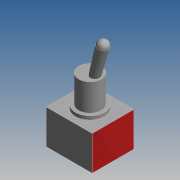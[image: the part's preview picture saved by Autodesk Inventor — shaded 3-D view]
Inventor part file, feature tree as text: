
AUTODESK INVENTOR PART (.ipt)
format: ipt  version: 2019 (Build 230136000, 136)  size: 237,056 bytes
history: native  units: mm
features: sketch x4, extrude x3, revolve x1, fillet x1
ambient origin geometry x8: Origin, YZ Plane, XZ Plane, XY Plane, X Axis, Y Axis, Z Axis, Center Point
bodies: Solid1 (feature_tree)
feature tree (9):
  extrude  "Extrusion1"  Depth=11.5mm
  extrude  "Extrusion2"  Depth=9.5mm
  extrude  "Extrusion3"  Depth=1.0mm
  revolve  "Revolution1"  Angle=15.0deg
  fillet  "Fillet1"  Radius=5.0mm
  sketch  "Sketch1"  dims[d0=12.7mm d1=11.5mm]
  sketch  "Sketch2"  dims[d2=9.5mm d3=0.0mm d4=8.0mm]
  sketch  "Sketch3"  dims[d5=1.0mm d6=0.0mm d7=6.2mm]
  sketch  "Sketch4"  dims[d8=7.5mm d9=0.0mm d10=15.0deg d11=5.0mm d13=10.0mm d14=3.0mm d16=2.5mm d17=90.0deg d18=1.4mm]
